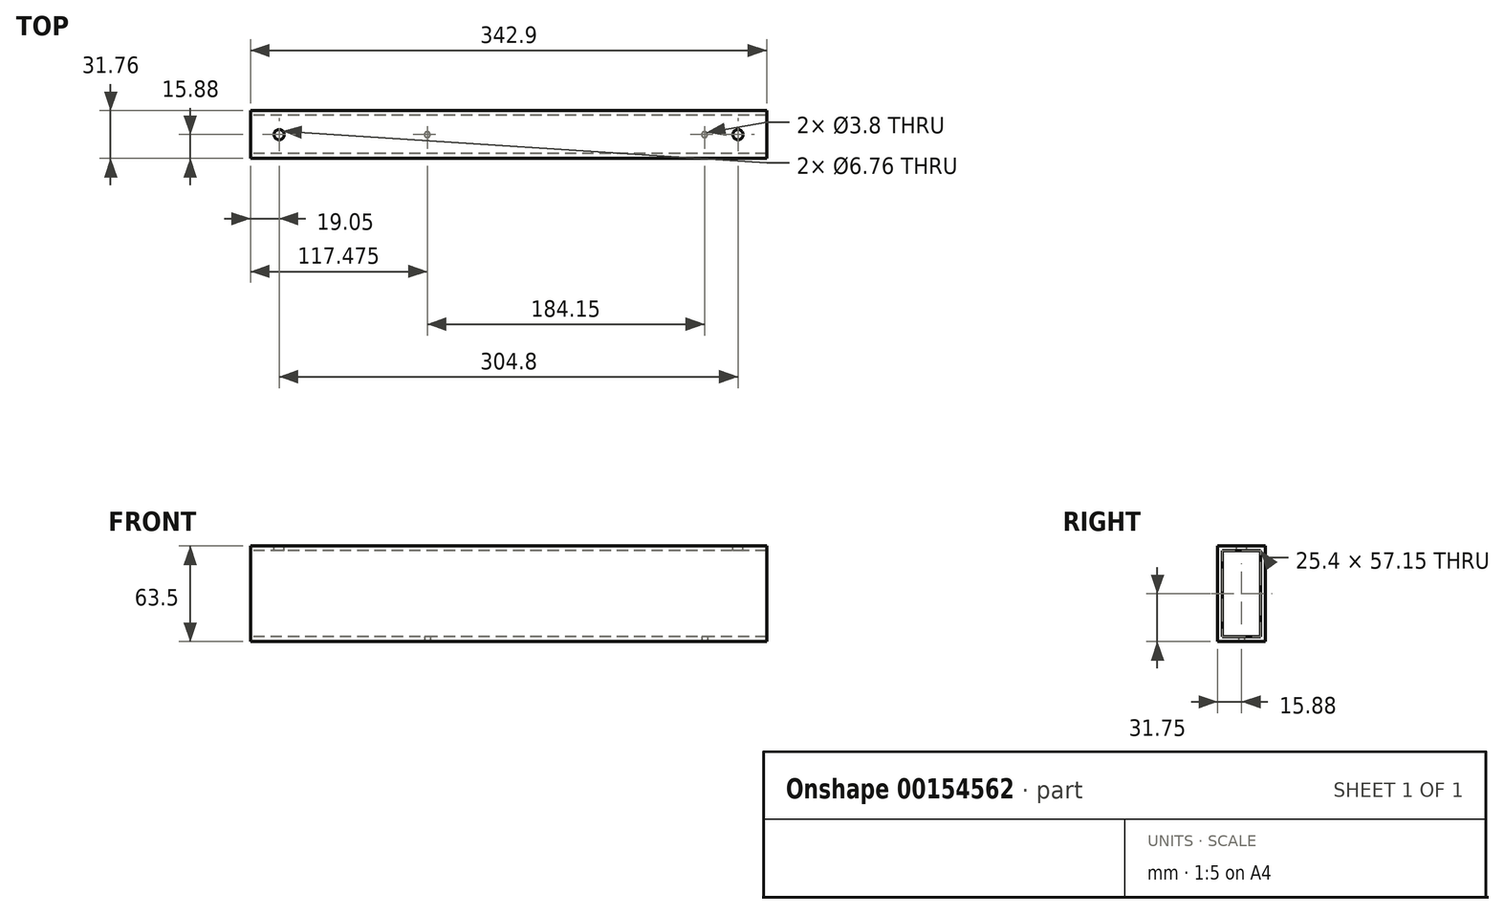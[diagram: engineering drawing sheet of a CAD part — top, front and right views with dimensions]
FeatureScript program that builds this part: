
annotation { "Feature Type Name" : "Feature", "Feature Type Description" : "" }
export const myFeature = defineFeature(function(context is Context, id is Id, definition is map)
    precondition{}
    {
        {
            var Q0;
            Q0=qCreatedBy(makeId("Right.planeOp"),FACE);
            var sketch = newSketch(context, id + "F0", { "sketchPlane" : qUnion([Q0])});
            skLineSegment(sketch, "E0.bottom", {"start": v(-15.87, 31.75) * mm, "end": v(15.88, 31.75) * mm});
            skLineSegment(sketch, "E0.top", {"start": v(-15.88, -31.75) * mm, "end": v(15.88, -31.75) * mm});
            skLineSegment(sketch, "E0.left", {"start": v(-15.87, 31.75) * mm, "end": v(-15.88, -31.75) * mm});
            skLineSegment(sketch, "E0.right", {"start": v(15.88, 31.75) * mm, "end": v(15.87, -31.75) * mm});
            skLineSegment(sketch, "E1.bottom", {"start": v(-12.7, 28.58) * mm, "end": v(12.7, 28.58) * mm});
            skLineSegment(sketch, "E1.top", {"start": v(-12.7, -28.58) * mm, "end": v(12.7, -28.58) * mm});
            skLineSegment(sketch, "E1.left", {"start": v(-12.7, 28.58) * mm, "end": v(-12.7, -28.58) * mm});
            skLineSegment(sketch, "E1.right", {"start": v(12.7, 28.58) * mm, "end": v(12.7, -28.58) * mm});
            skLineSegment(sketch, "E2", {"start": v(-12.7, 28.58) * mm, "end": v(12.7, -28.57) * mm, "construction": true});
            skSolve(sketch);
        }
        {
            var Q0;
            Q0=makeQuery(id+"F0.imprint","IMPRINT",FACE,{"disambiguationData":[TD([[makeQuery(id+"F0.imprint","IMPRINT",EDGE,{"derivedFrom":sQuery(id+"F0.wireOp",EDGE,"E0.bottom")}),-1.0]])]});
            extrude(context, id + "F1", {"entities" : qUnion([Q0]), "depth" : 342.9 * mm});
        }
        {
            var Q0;
            Q0=makeQuery(id+"F1.opExtrude","SWEPT_FACE",FACE,{"disambiguationData":[OSD([sQuery(id+"F0.wireOp",EDGE,"E0.top")])]});
            var sketch = newSketch(context, id + "F2", { "sketchPlane" : qUnion([Q0])});
            skLineSegment(sketch, "E3", {"start": v(0, 0) * mm, "end": v(342.9, 0) * mm, "construction": true});
            skLineSegment(sketch, "E4", {"start": v(117.48, 15.88) * mm, "end": v(117.48, -15.87) * mm, "construction": true});
            skLineSegment(sketch, "E5", {"start": v(301.63, 15.88) * mm, "end": v(301.63, -15.87) * mm, "construction": true});
            skCircle(sketch, "E6", {"center": v(117.48, 0) * mm, "radius": 1.9 * mm});
            skCircle(sketch, "E7", {"center": v(301.63, 0) * mm, "radius": 1.9 * mm});
            skSolve(sketch);
        }
        {
            var Q0;
            Q0=makeQuery(id+"F2.imprint","IMPRINT",FACE,{"disambiguationData":[TD([[makeQuery(id+"F2.imprint","IMPRINT",EDGE,{"derivedFrom":sQuery(id+"F2.wireOp",EDGE,"E6")}),1.0]])]});
            var Q1;
            Q1=makeQuery(id+"F2.imprint","IMPRINT",FACE,{"disambiguationData":[TD([[makeQuery(id+"F2.imprint","IMPRINT",EDGE,{"derivedFrom":sQuery(id+"F2.wireOp",EDGE,"E7")}),1.0]])]});
            extrude(context, id + "F3", {"entities" : qUnion([Q0, Q1]), "operationType" : NewBodyOperationType.REMOVE, "endBound" : BoundingType.UP_TO_NEXT, "oppositeDirection" : true, "depth" : 25.4 * mm});
        }
        {
            var Q0;
            Q0=makeQuery(id+"F1.opExtrude","SWEPT_FACE",FACE,{"disambiguationData":[OSD([sQuery(id+"F0.wireOp",EDGE,"E0.bottom")])]});
            var sketch = newSketch(context, id + "F4", { "sketchPlane" : qUnion([Q0])});
            skLineSegment(sketch, "E8", {"start": v(0, 0) * mm, "end": v(342.9, 0) * mm, "construction": true});
            skLineSegment(sketch, "E9", {"start": v(19.05, 15.88) * mm, "end": v(19.05, -15.87) * mm, "construction": true});
            skLineSegment(sketch, "E10", {"start": v(323.85, 15.88) * mm, "end": v(323.85, -15.87) * mm, "construction": true});
            skCircle(sketch, "E11", {"center": v(19.05, 0) * mm, "radius": 3.38 * mm});
            skCircle(sketch, "E12", {"center": v(323.85, 0) * mm, "radius": 3.38 * mm});
            skSolve(sketch);
        }
        {
            var Q0;
            Q0=makeQuery(id+"F4.imprint","IMPRINT",FACE,{"disambiguationData":[TD([[makeQuery(id+"F4.imprint","IMPRINT",EDGE,{"derivedFrom":sQuery(id+"F4.wireOp",EDGE,"E11")}),1.0]])]});
            var Q1;
            Q1=makeQuery(id+"F4.imprint","IMPRINT",FACE,{"disambiguationData":[TD([[makeQuery(id+"F4.imprint","IMPRINT",EDGE,{"derivedFrom":sQuery(id+"F4.wireOp",EDGE,"E12")}),1.0]])]});
            extrude(context, id + "F5", {"entities" : qUnion([Q0, Q1]), "operationType" : NewBodyOperationType.REMOVE, "endBound" : BoundingType.UP_TO_NEXT, "oppositeDirection" : true, "depth" : 25.4 * mm});
        }
    });
